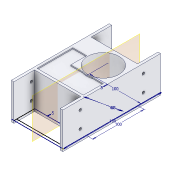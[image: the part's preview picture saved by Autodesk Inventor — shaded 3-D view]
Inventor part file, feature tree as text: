
AUTODESK INVENTOR PART (.ipt)
format: ipt  version: 2020.3 (Build 243373010, 373A)  size: 186,368 bytes
history: native  units: mm
features: extrude x8, sketch x5, hole x1, plane x1, mirror x1
ambient origin geometry x8: Origin, YZ Plane, XZ Plane, XY Plane, X Axis, Y Axis, Z Axis, Center Point
bodies: Solid1 (feature_tree)
feature tree (16):
  sketch  "Sketch1"  dims[d0=190.0mm d1=100.0mm]
  extrude  "Extrusion1"  Depth=100.0mm
  extrude  "Extrusion2"  Depth=5.0mm
  extrude  "Extrusion3"  Depth=65.0mm TaperAngle=0.0deg
  extrude  "Extrusion5"  Depth=65.0mm TaperAngle=0.0deg
  sketch  "Sketch2"  dims[d2=100.0mm d3=5.0mm]
  extrude  "Extrusion4"  Depth=65.0mm
  extrude  "Extrusion6"  Depth=65.0mm TaperAngle=0.0deg
  extrude  "Extrusion7"  Depth=65.0mm TaperAngle=0.0deg
  extrude  "Extrusion8"  Depth=3.0mm
  hole  "Hole1"  [1 undecoded]
  plane  "Work Plane1"
  mirror  "Mirror1"
  sketch  "Sketch3"  dims[d4=5.0mm d5=65.0mm d6=0.0mm]
  sketch  "Sketch4"  dims[d7=5.0mm d8=0.0mm d9=65.0mm d10=0.0mm]
  sketch  "Sketch5"  dims[d11=61.0mm d12=65.0mm d13=65.0mm d14=0.0mm d15=65.0mm d16=0.0mm d17=3.0mm d18=92.0mm d19=0.0mm d20=66.5mm d21=0.0mm d22=2.0mm d23=0.0mm d24=16.723mm d25=32.0mm d26=4.917mm d27=12.0mm d28=4.0mm d29=2.0mm d30=90.0deg d31=17.1mm d32=0.0mm]
note: 1 required parameter value undecoded (feature->parameter linkage not recoverable at this tier; creation-order binding heuristic only, values carry confidence <= 0.55)
